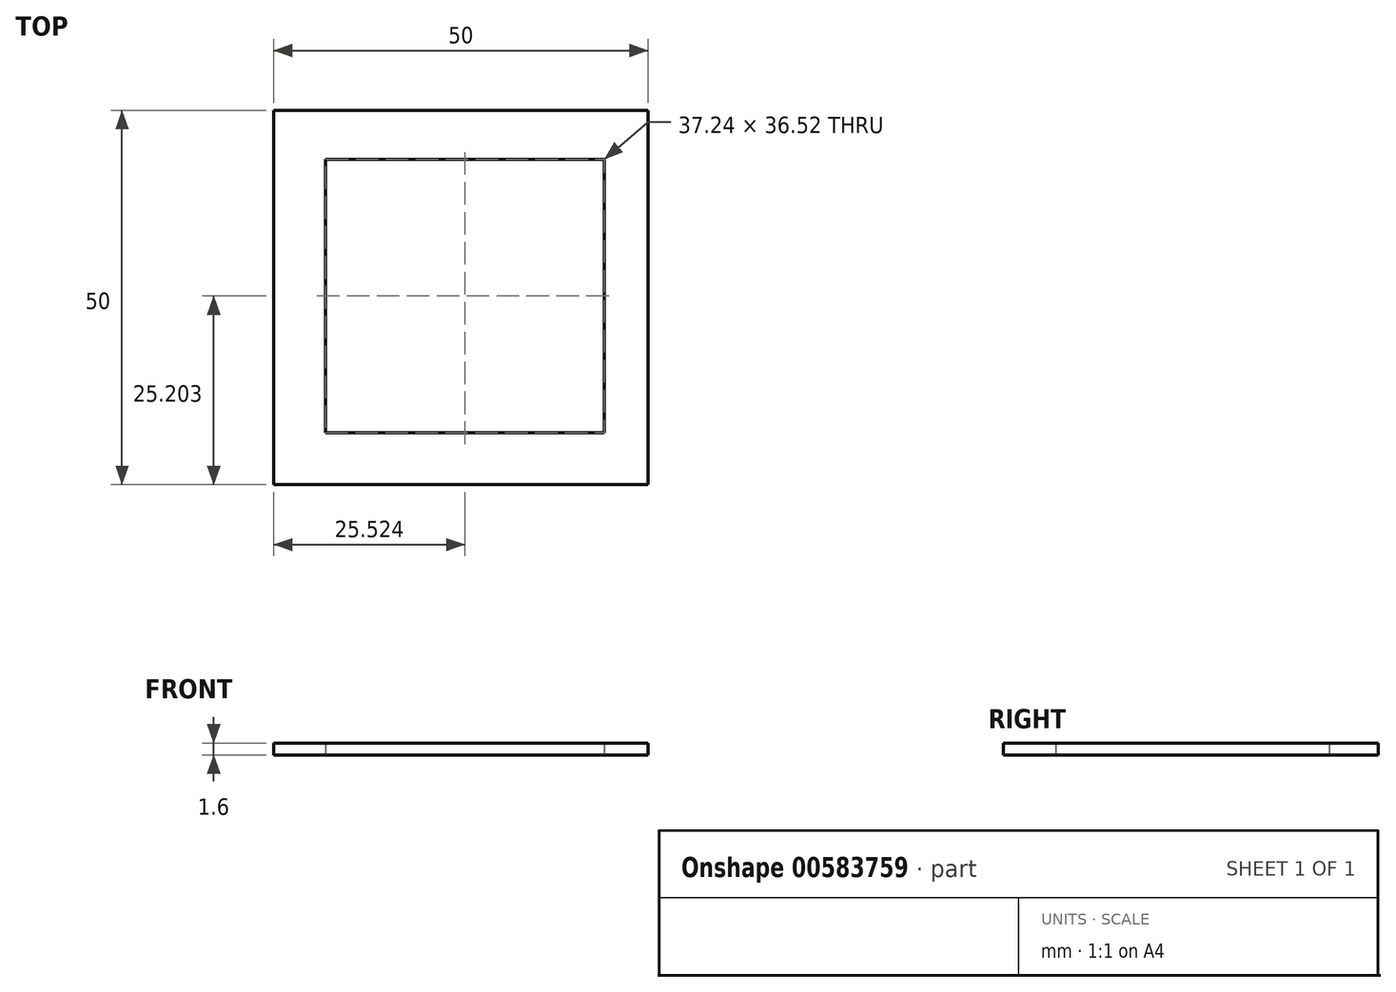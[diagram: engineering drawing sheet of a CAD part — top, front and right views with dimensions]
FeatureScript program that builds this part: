
annotation { "Feature Type Name" : "Feature", "Feature Type Description" : "" }
export const myFeature = defineFeature(function(context is Context, id is Id, definition is map)
    precondition{}
    {
        {
            var Q0;
            Q0=qCreatedBy(makeId("Top.planeOp"),FACE);
            var sketch = newSketch(context, id + "F0", { "sketchPlane" : qUnion([Q0])});
            skLineSegment(sketch, "E0.bottom", {"start": v(0, 0) * mm, "end": v(50, 0) * mm});
            skLineSegment(sketch, "E0.top", {"start": v(0, -50) * mm, "end": v(50, -50) * mm});
            skLineSegment(sketch, "E0.left", {"start": v(0, 0) * mm, "end": v(0, -50) * mm});
            skLineSegment(sketch, "E0.right", {"start": v(50, 0) * mm, "end": v(50, -50) * mm});
            skLineSegment(sketch, "E1.bottom", {"start": v(6.9, -6.54) * mm, "end": v(44.14, -6.54) * mm});
            skLineSegment(sketch, "E1.top", {"start": v(6.9, -43.05) * mm, "end": v(44.14, -43.05) * mm});
            skLineSegment(sketch, "E1.left", {"start": v(6.9, -6.54) * mm, "end": v(6.9, -43.05) * mm});
            skLineSegment(sketch, "E1.right", {"start": v(44.14, -6.54) * mm, "end": v(44.14, -43.05) * mm});
            skSolve(sketch);
        }
        {
            var Q0;
            Q0 = qSketchRegion(id + "F0", true);
            extrude(context, id + "F1", {"entities" : qUnion([Q0]), "depth" : 1.6 * mm, "offsetDistance" : 25 * mm});
        }
    });
